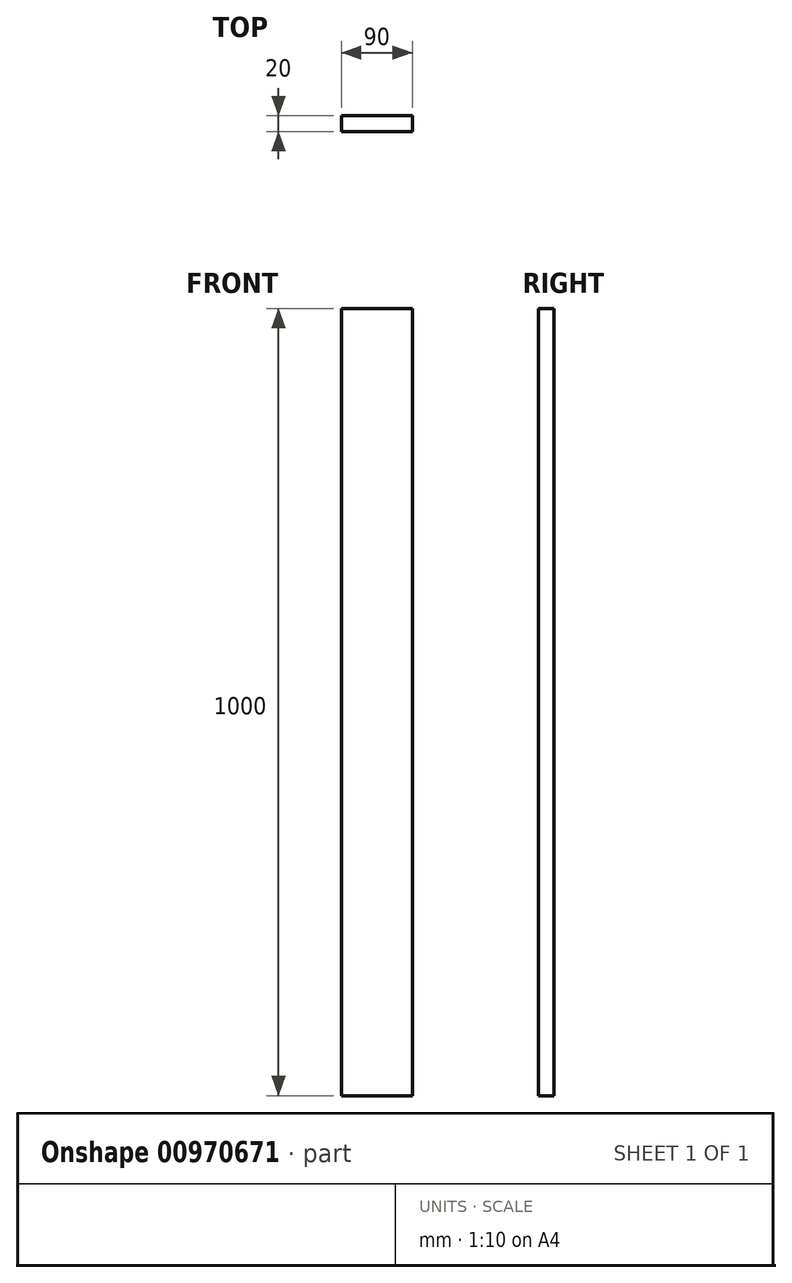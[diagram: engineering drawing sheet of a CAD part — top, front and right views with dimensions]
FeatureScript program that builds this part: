
annotation { "Feature Type Name" : "Feature", "Feature Type Description" : "" }
export const myFeature = defineFeature(function(context is Context, id is Id, definition is map)
    precondition{}
    {
        {
            var Q0;
            Q0=qCreatedBy(makeId("Top.planeOp"),FACE);
            var sketch = newSketch(context, id + "F0", { "sketchPlane" : qUnion([Q0])});
            skLineSegment(sketch, "E0.bottom", {"start": v(-14.6, 3.03) * mm, "end": v(75.4, 3.03) * mm});
            skLineSegment(sketch, "E0.top", {"start": v(-14.6, -16.97) * mm, "end": v(75.4, -16.97) * mm});
            skLineSegment(sketch, "E0.left", {"start": v(-14.6, 3.03) * mm, "end": v(-14.6, -16.97) * mm});
            skLineSegment(sketch, "E0.right", {"start": v(75.4, 3.03) * mm, "end": v(75.4, -16.97) * mm});
            skSolve(sketch);
        }
        {
            var Q0;
            Q0 = qSketchRegion(id + "F0", true);
            extrude(context, id + "F1", {"entities" : qUnion([Q0]), "depth" : 1000 * mm, "offsetDistance" : 25 * mm});
        }
    });
